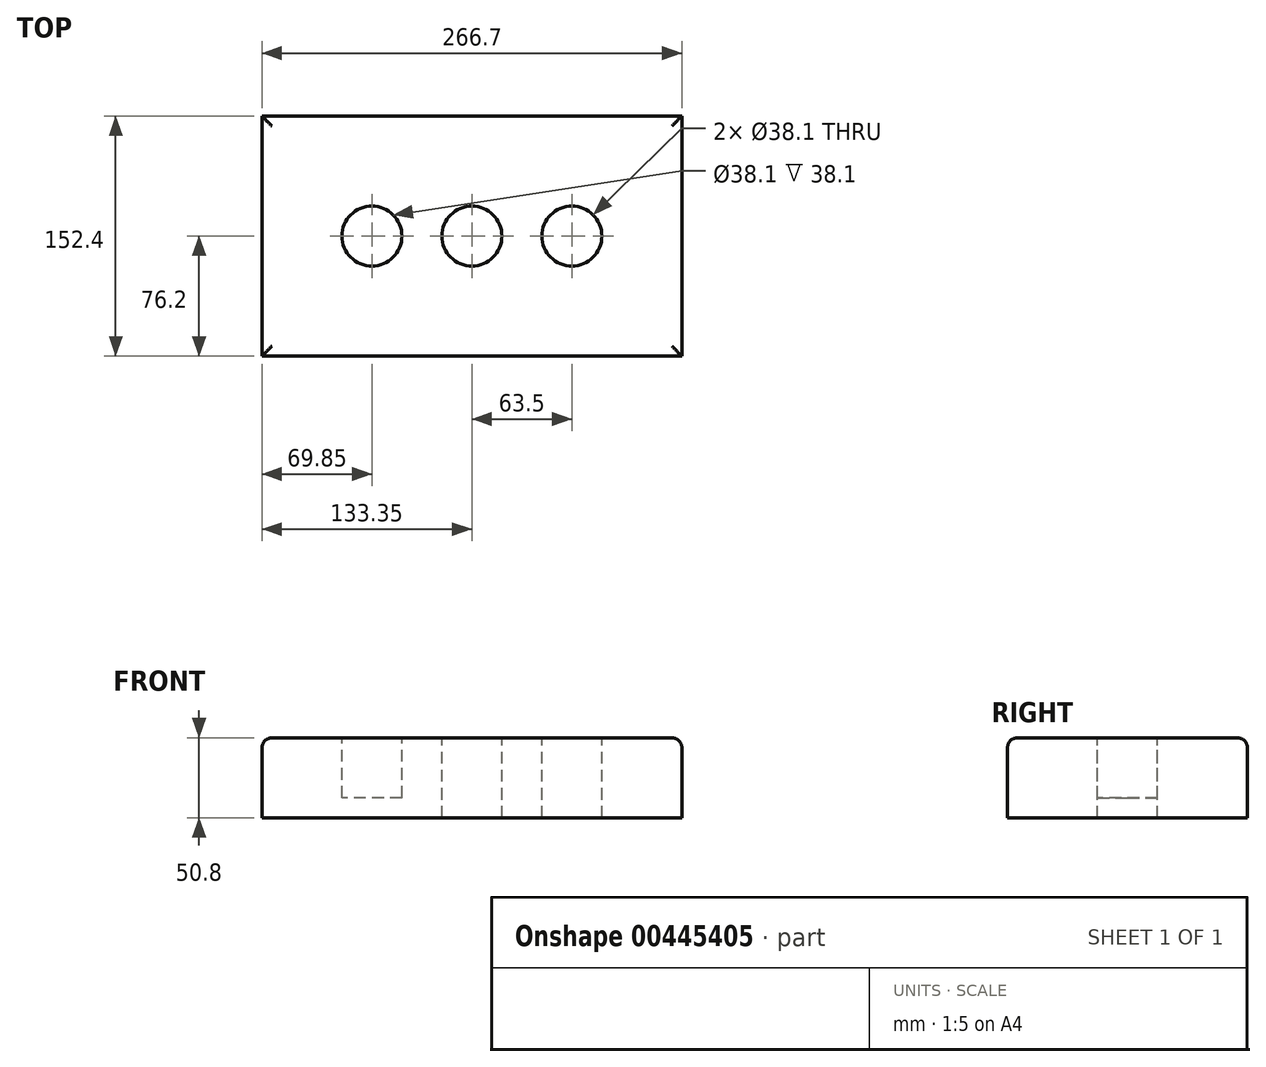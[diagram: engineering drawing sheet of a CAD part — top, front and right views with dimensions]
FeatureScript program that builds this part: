
annotation { "Feature Type Name" : "Feature", "Feature Type Description" : "" }
export const myFeature = defineFeature(function(context is Context, id is Id, definition is map)
    precondition{}
    {
        {
            var Q0;
            Q0=qCreatedBy(makeId("Top.planeOp"),FACE);
            var sketch = newSketch(context, id + "F0", { "sketchPlane" : qUnion([Q0])});
            skLineSegment(sketch, "E0.bottom", {"start": v(133.35, -76.2) * mm, "end": v(-133.35, -76.2) * mm});
            skLineSegment(sketch, "E0.top", {"start": v(133.35, 76.2) * mm, "end": v(-133.35, 76.2) * mm});
            skLineSegment(sketch, "E0.left", {"start": v(133.35, -76.2) * mm, "end": v(133.35, 76.2) * mm});
            skLineSegment(sketch, "E0.right", {"start": v(-133.35, -76.2) * mm, "end": v(-133.35, 76.2) * mm});
            skPoint(sketch, "E0.middle", {"position": v(0, 0) * mm});
            skSolve(sketch);
        }
        {
            var Q0;
            Q0=makeQuery(id+"F0.imprint","IMPRINT",FACE,{"disambiguationData":[TD([[makeQuery(id+"F0.imprint","IMPRINT",EDGE,{"derivedFrom":sQuery(id+"F0.wireOp",EDGE,"E0.bottom")}),-1.0]])]});
            extrude(context, id + "F1", {"entities" : qUnion([Q0]), "depth" : 50.8 * mm});
        }
        {
            var Q0;
            Q0=makeQuery(id+"F1.opExtrude","CAP_FACE",FACE,{"disambiguationData":[OSD([sQuery(id+"F0.wireOp",EDGE,"E0.bottom"),sQuery(id+"F0.wireOp",EDGE,"E0.top"),sQuery(id+"F0.wireOp",EDGE,"E0.left"),sQuery(id+"F0.wireOp",EDGE,"E0.right")])],"isStart":false});
            var sketch = newSketch(context, id + "F2", { "sketchPlane" : qUnion([Q0])});
            skCircle(sketch, "E1", {"center": v(0, 0) * mm, "radius": 19.05 * mm});
            skPoint(sketch, "E2", {"position": v(63.5, 0) * mm});
            skCircle(sketch, "E3", {"center": v(63.5, 0) * mm, "radius": 19.05 * mm});
            skPoint(sketch, "E4", {"position": v(-63.5, 0) * mm});
            skCircle(sketch, "E5", {"center": v(-63.5, 0) * mm, "radius": 19.05 * mm});
            skSolve(sketch);
        }
        {
            var Q0;
            Q0=makeQuery(id+"F2.imprint","IMPRINT",FACE,{"disambiguationData":[TD([[makeQuery(id+"F2.imprint","IMPRINT",EDGE,{"derivedFrom":sQuery(id+"F2.wireOp",EDGE,"E5")}),1.0]])]});
            var Q1;
            Q1=makeQuery(id+"F2.imprint","IMPRINT",FACE,{"disambiguationData":[TD([[makeQuery(id+"F2.imprint","IMPRINT",EDGE,{"derivedFrom":sQuery(id+"F2.wireOp",EDGE,"E1")}),1.0]])]});
            var Q2;
            Q2=makeQuery(id+"F2.imprint","IMPRINT",FACE,{"disambiguationData":[TD([[makeQuery(id+"F2.imprint","IMPRINT",EDGE,{"derivedFrom":sQuery(id+"F2.wireOp",EDGE,"E3")}),1.0]])]});
            extrude(context, id + "F3", {"entities" : qUnion([Q0, Q1, Q2]), "operationType" : NewBodyOperationType.REMOVE, "oppositeDirection" : true, "depth" : 38.1 * mm});
        }
        {
            var Q0;
            Q0=makeQuery(id+"F1.opExtrude","CAP_EDGE",EDGE,{"disambiguationData":[OSD([sQuery(id+"F0.wireOp",EDGE,"E0.left")])],"isStart":false});
            var Q1;
            Q1=makeQuery(id+"F1.opExtrude","CAP_EDGE",EDGE,{"disambiguationData":[OSD([sQuery(id+"F0.wireOp",EDGE,"E0.top")])],"isStart":false});
            var Q2;
            Q2=makeQuery(id+"F1.opExtrude","CAP_EDGE",EDGE,{"disambiguationData":[OSD([sQuery(id+"F0.wireOp",EDGE,"E0.bottom")])],"isStart":false});
            var Q3;
            Q3=makeQuery(id+"F1.opExtrude","CAP_EDGE",EDGE,{"disambiguationData":[OSD([sQuery(id+"F0.wireOp",EDGE,"E0.right")])],"isStart":false});
            fillet(context, id + "F4", {"entities" : qUnion([Q0, Q1, Q2, Q3]), "radius" : 6.35 * mm, "tangentPropagation" : true, "allowEdgeOverflow" : false});
        }
        {
            var Q0;
            Q0=makeQuery(id+"F3.boolean.opBoolean","COPY",FACE,{"derivedFrom":makeQuery(id+"F3.opExtrude","CAP_FACE",FACE,{"disambiguationData":[OSD([sQuery(id+"F2.wireOp",EDGE,"E1")])],"isStart":false})});
            var Q1;
            Q1=makeQuery(id+"F3.boolean.opBoolean","COPY",FACE,{"derivedFrom":makeQuery(id+"F3.opExtrude","CAP_FACE",FACE,{"disambiguationData":[OSD([sQuery(id+"F2.wireOp",EDGE,"E3")])],"isStart":false})});
            extrude(context, id + "F5", {"entities" : qUnion([Q0, Q1]), "operationType" : NewBodyOperationType.REMOVE, "oppositeDirection" : true, "depth" : 50.8 * mm});
        }
    });
